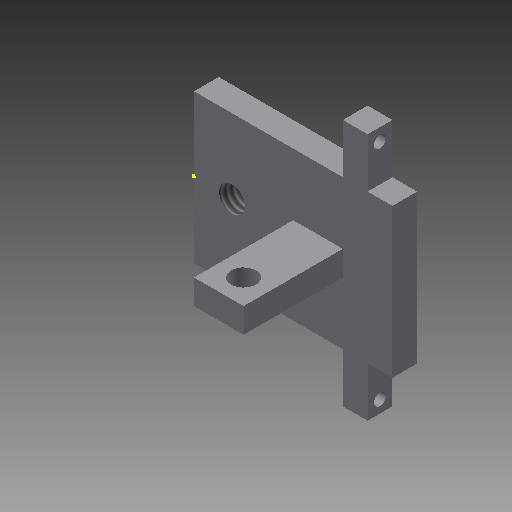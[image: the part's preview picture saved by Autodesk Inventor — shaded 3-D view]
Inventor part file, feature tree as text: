
AUTODESK INVENTOR PART (.ipt)
format: ipt  version: 2017 (Build 210142000, 142)  size: 151,040 bytes
history: native  units: in
note: dims shown in document units (in); Inventor stores cm internally (conversion verified against a paired STEP export)
features: sketch x7, hole x4, extrude x3, projected_geometry x2
ambient origin geometry x8: Origin, YZ Plane, XZ Plane, XY Plane, X Axis, Y Axis, Z Axis, Center Point
bodies: Solid1 (feature_tree)
feature tree (16):
  extrude  "Extrusion1"  Depth=1.0in
  extrude  "Extrusion2"  Depth=0.25in
  hole  "Hole1"  [1 undecoded]
  hole  "Hole3"  [1 undecoded]
  sketch  "Sketch6"  dims[d12=0.25in d13=0.5in d14=0.0in]
  sketch  "Sketch7"  dims[d15=0.06in d16=0.75in d17=0.375in d18=0.25in d19=0.5635in d20=1.0in d21=0.8108in d22=0.125in]
  extrude  "Extrusion3"  Depth=0.5in TaperAngle=0.0deg
  hole  "Hole4"  [1 undecoded]
  hole  "Hole5"  [1 undecoded]
  sketch  "Sketch1"  dims[d0=0.75in d2=1.0in]
  sketch  "Sketch2"  dims[d3=0.125in d4=0.25in]
  sketch  "Sketch3"  dims[d5=0.125in d6=0.0in d7=0.125in]
  projected_geometry  "Projected Loop1"
  sketch  "Sketch5"  dims[d10=0.25in d11=0.3125in]
  projected_geometry  "Projected Loop3"
  sketch  "Sketch8"  dims[d30=0.13in d31=0.75in d32=0.375in d33=0.25in d34=0.5635in d35=1.0in d36=0.8108in d37=0.125in d38=0.063in d39=0.25in d40=0.0in d41=0.0625in d42=0.0625in d43=0.06in d44=0.75in d45=0.375in d46=0.25in d47=0.5635in d48=1.0in d49=0.8108in d50=0.125in d51=0.125in d52=0.125in d53=0.75in d54=0.375in d55=0.25in d56=0.5635in d57=1.0in d58=0.8108in]
note: 4 required parameter values undecoded (feature->parameter linkage not recoverable at this tier; creation-order binding heuristic only, values carry confidence <= 0.55)
